# Revit family: Crealco Evolution F
name_source: partatom
category: Windows
revit_build: Autodesk Revit 2016 (Build: 20150714_1515(x64)
units: mm (PartAtom-declared; Revit-internal decimal feet)

## family parameters
Always vertical = Yes
Cut with Voids When Loaded = No
Host = Wall
OmniClass Number = 23.30.20.00
OmniClass Title = Windows
Room Calculation Point = No
Shared = No

## types (3) — shared parameters
54mm Mullion Inertia = 12.55
75mm Mullion Inertia = 31
Default Sill Height = 800 mm  [stored 2.62467 ft]
Description = Bottom Hung Open In Window
Fixed Panel Top Gap = 27 mm  [stored 0.0885827 ft]
Limit Fixed Panel Height Max = 6000 mm  [stored 19.685 ft]
Limit Fixed Panel Height Min = 100 mm  [stored 0.328084 ft]
Limit Glazing Thickness Max = 6 mm  [stored 0.019685 ft]
Limit Glazing Thickness Min = 4 mm  [stored 0.0131234 ft]
Limit Mullion 1 Spacing Min = 230 mm  [stored 0.754593 ft]
Limit Mullion 2 Spacing Max = 870 mm
Limit Mullion 2 Spacing Min = 220 mm  [stored 0.721785 ft]
Limit Sash Height Max = 700 mm  [stored 2.29659 ft]
Limit Sash Height Min = 200 mm  [stored 0.656168 ft]
Limit Sash Width Max = 850 mm  [stored 2.78871 ft]
Limit Sash Width Min = 200 mm  [stored 0.656168 ft]
Limit Window Height Max = 6775 mm
Limit Window Height Min = 375 mm  [stored 1.23031 ft]
Limit Window Width Max = 2630 mm  [stored 8.62861 ft]
Limit Window Width Min = 680 mm
Manufacturer = Crealco
Max Wind Load = 10000
Model = Evolution
Mullion Width = 20 mm  [stored 0.0656168 ft]
Sash Mullion Gap = 10 mm  [stored 0.0328084 ft]
Sash Offset = 5 mm  [stored 0.0164042 ft]
Sash Side Gap = 20 mm  [stored 0.0656168 ft]
Standard Mullion Inertia = 2.36
Standard Width = 2632 mm  [stored 8.63517 ft]
Transom Fixed Panel Gap = 18 mm
Transom Mullion Side Gap = 18 mm
Transom Side Gap = 27 mm  [stored 0.0885827 ft]
URL = https://www.crealco.co.za
Wall Closure = By host
zero-valued in all types: Min Wind Load

## per-type parameters (varying)
| type | 75mm Mullion | Standard Height | Standard Size | Standard Transom Top Gap | Type Comments |
| 2632 x 0890mm (EVOL-2609TB) | No | 890 mm  [stored 2.91995 ft] | Yes | 295 mm  [stored 0.967848 ft] | EVOL-2609TB |
| User Defined | Yes | 832 mm  [stored 2.72966 ft] | No | 295 mm  [stored 0.967848 ft] | Custom |
| 2632 x 1190mm (EVOL-2612TB) | No | 1190 mm  [stored 3.9042 ft] | Yes | 595 mm  [stored 1.9521 ft] | EVOL-2612TB |

note: [stored X ft] marks values corroborated as IEEE doubles in the binary element streams (Revit-internal decimal feet)

## geometry (parser evidence)
native form markers: Sweep x19
no freeform markers — native parametric forms only
